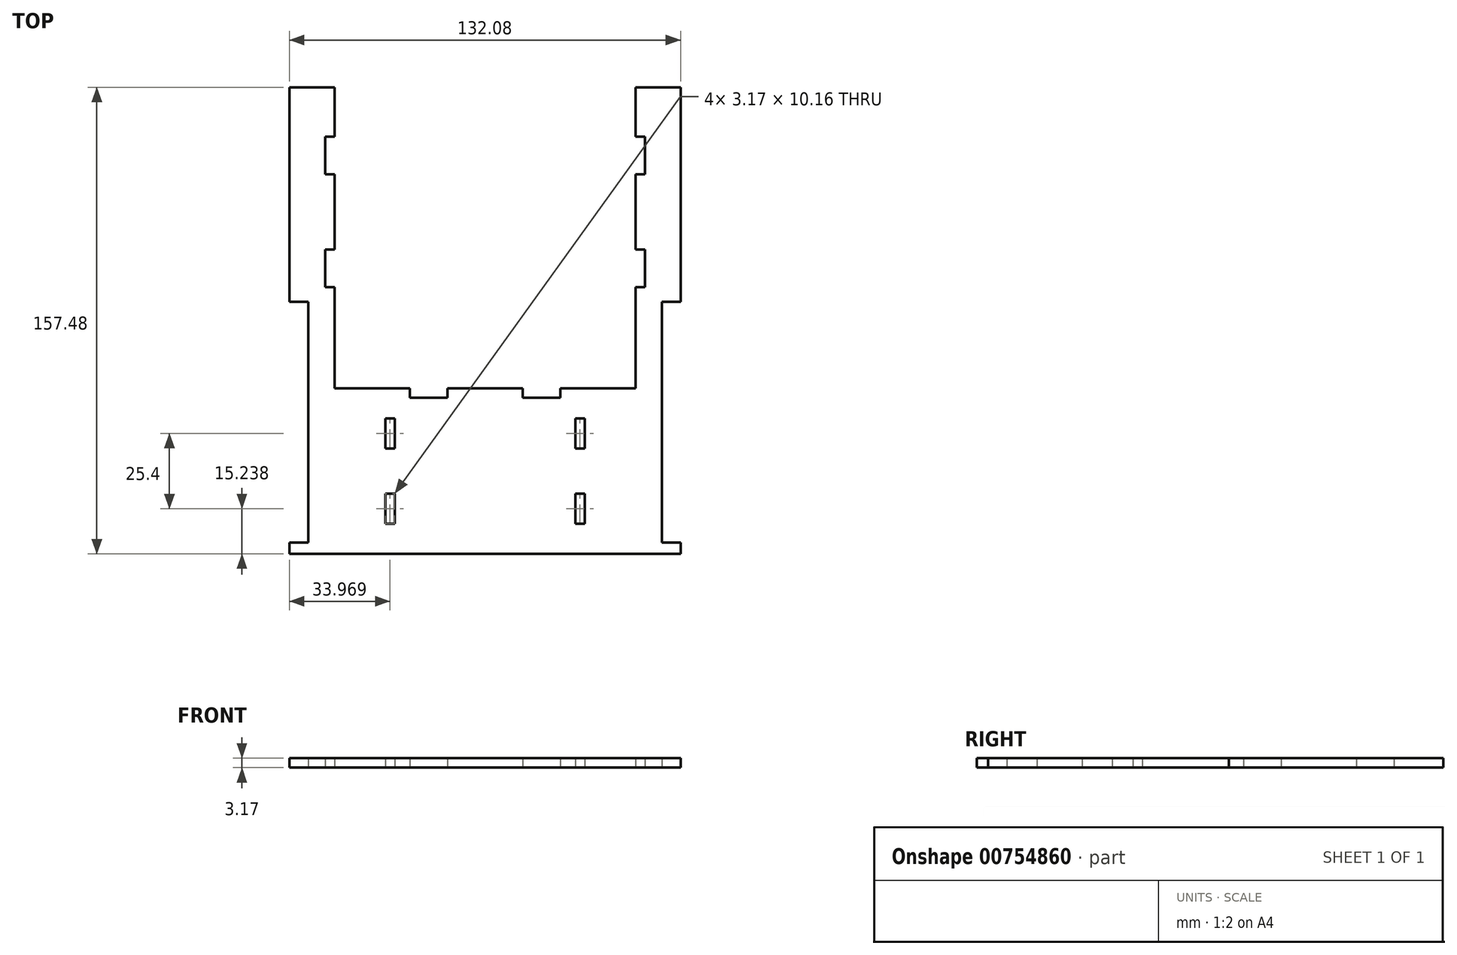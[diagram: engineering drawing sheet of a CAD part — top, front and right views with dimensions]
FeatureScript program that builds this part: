
annotation { "Feature Type Name" : "Feature", "Feature Type Description" : "" }
export const myFeature = defineFeature(function(context is Context, id is Id, definition is map)
    precondition{}
    {
        {
            var Q0;
            Q0=qCreatedBy(makeId("Top.planeOp"),FACE);
            var sketch = newSketch(context, id + "F0", { "sketchPlane" : qUnion([Q0])});
            skLineSegment(sketch, "E0.top", {"start": v(-138.04, -64.06) * mm, "end": v(-5.96, -64.06) * mm});
            skLineSegment(sketch, "E0.left", {"start": v(-138.04, 93.42) * mm, "end": v(-138.04, 21.05) * mm});
            skLineSegment(sketch, "E0.right", {"start": v(-5.96, 93.42) * mm, "end": v(-5.96, 21.05) * mm});
            skLineSegment(sketch, "E1", {"start": v(-122.8, 93.42) * mm, "end": v(-122.8, 76.78) * mm});
            skLineSegment(sketch, "E2", {"start": v(-122.8, -8.18) * mm, "end": v(-97.4, -8.18) * mm});
            skLineSegment(sketch, "E3.MirrorCS", {"start": v(-26.57, -8.18) * mm, "end": v(-46.6, -8.18) * mm});
            skLineSegment(sketch, "E4.MirrorCS", {"start": v(-21.2, 93.42) * mm, "end": v(-21.2, 76.78) * mm});
            skPoint(sketch, "E5.orphan", {"position": v(-72, 108.66) * mm});
            skPoint(sketch, "E6.end.orphan", {"position": v(-72, -64.06) * mm});
            skLineSegment(sketch, "E7.bottom", {"start": v(-41.52, -18.34) * mm, "end": v(-38.35, -18.34) * mm});
            skLineSegment(sketch, "E7.top", {"start": v(-41.52, -28.5) * mm, "end": v(-38.35, -28.5) * mm});
            skLineSegment(sketch, "E7.left", {"start": v(-41.52, -18.34) * mm, "end": v(-41.52, -28.5) * mm});
            skLineSegment(sketch, "E7.right", {"start": v(-38.35, -18.34) * mm, "end": v(-38.35, -28.5) * mm});
            skLineSegment(sketch, "E8.bottom", {"start": v(-41.52, -43.74) * mm, "end": v(-38.35, -43.74) * mm});
            skLineSegment(sketch, "E8.top", {"start": v(-41.52, -53.9) * mm, "end": v(-38.35, -53.9) * mm});
            skLineSegment(sketch, "E8.left", {"start": v(-41.52, -43.74) * mm, "end": v(-41.52, -53.9) * mm});
            skLineSegment(sketch, "E8.right", {"start": v(-38.35, -43.74) * mm, "end": v(-38.35, -53.9) * mm});
            skLineSegment(sketch, "E9.MirrorCS", {"start": v(-102.48, -18.34) * mm, "end": v(-102.48, -28.5) * mm});
            skLineSegment(sketch, "E10.MirrorCS", {"start": v(-102.48, -43.74) * mm, "end": v(-102.48, -53.9) * mm});
            skLineSegment(sketch, "E11.MirrorCS", {"start": v(-105.66, -43.74) * mm, "end": v(-105.66, -53.9) * mm});
            skLineSegment(sketch, "E12", {"start": v(-105.66, -18.34) * mm, "end": v(-102.48, -18.34) * mm});
            skLineSegment(sketch, "E13", {"start": v(-105.66, -28.5) * mm, "end": v(-102.48, -28.5) * mm});
            skLineSegment(sketch, "E14", {"start": v(-105.66, -43.74) * mm, "end": v(-102.48, -43.74) * mm});
            skLineSegment(sketch, "E15", {"start": v(-105.66, -53.9) * mm, "end": v(-102.48, -53.9) * mm});
            skLineSegment(sketch, "E16", {"start": v(-105.66, -18.34) * mm, "end": v(-105.66, -28.5) * mm});
            skPoint(sketch, "E17.orphan", {"position": v(-116.39, -28.5) * mm});
            skLineSegment(sketch, "E18", {"start": v(-26.57, -8.18) * mm, "end": v(-21.2, -8.18) * mm});
            skLineSegment(sketch, "E19.bottom", {"start": v(-5.96, 21.05) * mm, "end": v(-12.31, 21.05) * mm});
            skLineSegment(sketch, "E19.top", {"start": v(-5.96, -60.23) * mm, "end": v(-12.31, -60.23) * mm});
            skLineSegment(sketch, "E19.right", {"start": v(-12.31, 21.05) * mm, "end": v(-12.31, -60.23) * mm});
            skLineSegment(sketch, "E20", {"start": v(-72, -64.06) * mm, "end": v(-72, 50.3) * mm});
            skLineSegment(sketch, "E21.MirrorCS", {"start": v(-138.04, 21.05) * mm, "end": v(-131.7, 21.05) * mm});
            skLineSegment(sketch, "E22.MirrorCS", {"start": v(-131.7, 21.05) * mm, "end": v(-131.7, -60.23) * mm});
            skLineSegment(sketch, "E23.MirrorCS", {"start": v(-138.04, -60.23) * mm, "end": v(-131.7, -60.23) * mm});
            skLineSegment(sketch, "E24.trimOffspring", {"start": v(-138.04, -60.23) * mm, "end": v(-138.04, -64.06) * mm});
            skLineSegment(sketch, "E25.trimOffspring", {"start": v(-5.96, -60.23) * mm, "end": v(-5.96, -64.06) * mm});
            skLineSegment(sketch, "E26", {"start": v(-21.2, 93.42) * mm, "end": v(-5.96, 93.42) * mm});
            skLineSegment(sketch, "E27", {"start": v(-122.8, 93.42) * mm, "end": v(-138.04, 93.42) * mm});
            skPoint(sketch, "E0.bottom.start.orphan", {"position": v(-138.04, 108.66) * mm});
            skPoint(sketch, "E28.orphan", {"position": v(-122.8, 108.66) * mm});
            skPoint(sketch, "E29.trimOffspring.start.orphan", {"position": v(-21.2, 108.66) * mm});
            skPoint(sketch, "E30.orphan", {"position": v(-5.96, 108.66) * mm});
            skLineSegment(sketch, "E31", {"start": v(-72, -64.06) * mm, "end": v(-72, 126.89) * mm});
            skLineSegment(sketch, "E32.top", {"start": v(-97.4, -11.36) * mm, "end": v(-84.7, -11.36) * mm});
            skLineSegment(sketch, "E32.left", {"start": v(-97.4, -8.18) * mm, "end": v(-97.4, -11.36) * mm});
            skLineSegment(sketch, "E32.right", {"start": v(-84.7, -8.18) * mm, "end": v(-84.7, -11.36) * mm});
            skLineSegment(sketch, "E33.MirrorCS", {"start": v(-46.6, -11.36) * mm, "end": v(-59.3, -11.36) * mm});
            skLineSegment(sketch, "E34", {"start": v(-59.3, -11.36) * mm, "end": v(-59.3, -8.18) * mm});
            skLineSegment(sketch, "E35", {"start": v(-46.6, -11.36) * mm, "end": v(-46.6, -8.18) * mm});
            skLineSegment(sketch, "E36.bottom", {"start": v(-122.8, 76.78) * mm, "end": v(-125.98, 76.78) * mm});
            skLineSegment(sketch, "E36.top", {"start": v(-122.8, 64.08) * mm, "end": v(-125.98, 64.08) * mm});
            skLineSegment(sketch, "E36.right", {"start": v(-125.98, 76.78) * mm, "end": v(-125.98, 64.08) * mm});
            skLineSegment(sketch, "E37.bottom", {"start": v(-122.8, 38.68) * mm, "end": v(-125.98, 38.68) * mm});
            skLineSegment(sketch, "E37.top", {"start": v(-122.8, 25.98) * mm, "end": v(-125.98, 25.98) * mm});
            skLineSegment(sketch, "E37.right", {"start": v(-125.98, 38.68) * mm, "end": v(-125.98, 25.98) * mm});
            skLineSegment(sketch, "E38.MirrorCS", {"start": v(-18.03, 76.78) * mm, "end": v(-18.03, 64.08) * mm});
            skLineSegment(sketch, "E39.MirrorCS", {"start": v(-18.03, 38.68) * mm, "end": v(-18.03, 25.98) * mm});
            skLineSegment(sketch, "E40", {"start": v(-18.03, 76.78) * mm, "end": v(-21.2, 76.78) * mm});
            skLineSegment(sketch, "E41", {"start": v(-18.03, 64.08) * mm, "end": v(-21.2, 64.08) * mm});
            skLineSegment(sketch, "E42", {"start": v(-18.03, 38.68) * mm, "end": v(-21.2, 38.68) * mm});
            skLineSegment(sketch, "E43", {"start": v(-18.03, 25.98) * mm, "end": v(-21.2, 25.98) * mm});
            skLineSegment(sketch, "E44.trimOffspring", {"start": v(-122.8, 64.08) * mm, "end": v(-122.8, 38.68) * mm});
            skLineSegment(sketch, "E45.trimOffspring", {"start": v(-122.8, 25.98) * mm, "end": v(-122.8, -8.18) * mm});
            skLineSegment(sketch, "E46.trimOffspring", {"start": v(-21.2, 64.08) * mm, "end": v(-21.2, 38.68) * mm});
            skLineSegment(sketch, "E47.trimOffspring", {"start": v(-21.2, 25.98) * mm, "end": v(-21.2, -8.18) * mm});
            skLineSegment(sketch, "E48.trimOffspring", {"start": v(-84.7, -8.18) * mm, "end": v(-72, -8.18) * mm});
            skLineSegment(sketch, "E49.trimOffspring", {"start": v(-59.3, -8.18) * mm, "end": v(-77.37, -8.18) * mm});
            skSolve(sketch);
        }
        {
            var Q0;
            Q0 = qSketchRegion(id + "F0", true);
            extrude(context, id + "F1", {"entities" : qUnion([Q0]), "depth" : 3.17 * mm, "offsetDistance" : 25.4 * mm});
        }
    });
